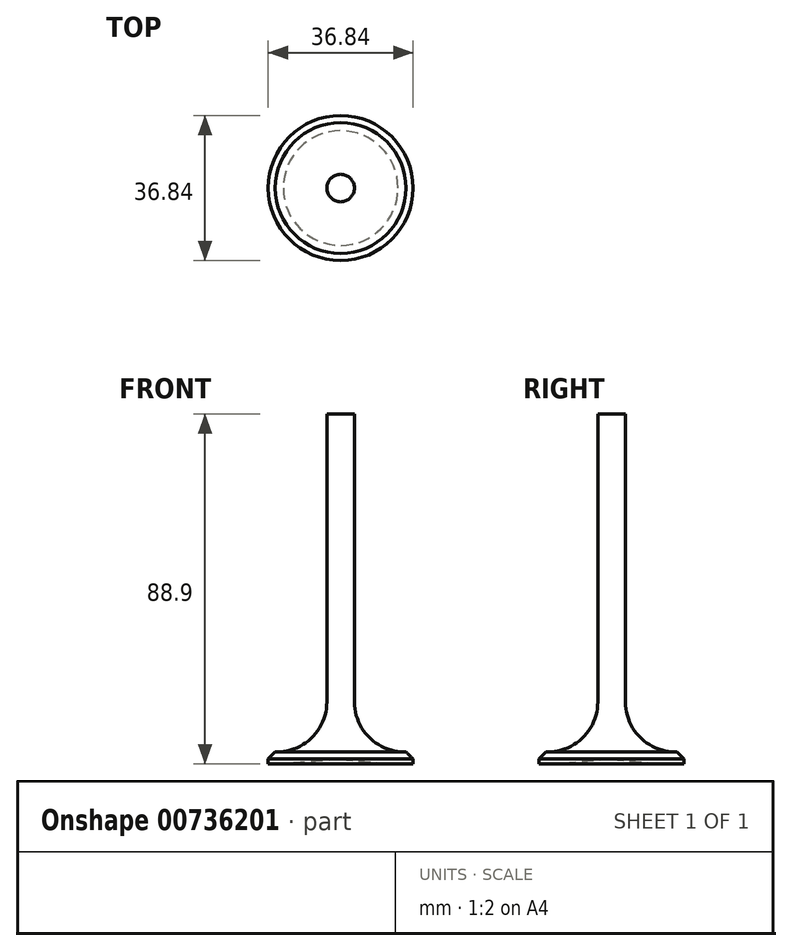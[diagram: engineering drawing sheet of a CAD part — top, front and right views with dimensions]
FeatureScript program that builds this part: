
annotation { "Feature Type Name" : "Feature", "Feature Type Description" : "" }
export const myFeature = defineFeature(function(context is Context, id is Id, definition is map)
    precondition{}
    {
        {
            var Q0;
            Q0=qCreatedBy(makeId("Front.planeOp"),FACE);
            var sketch = newSketch(context, id + "F0", { "sketchPlane" : qUnion([Q0])});
            skLineSegment(sketch, "E0", {"start": v(-14.56, 0) * mm, "end": v(-18.41, 0) * mm});
            skLineSegment(sketch, "E1", {"start": v(-18.41, 0) * mm, "end": v(-18.41, 1.27) * mm});
            skLineSegment(sketch, "E2", {"start": v(-18.41, 1.27) * mm, "end": v(-16.62, 3.07) * mm});
            skLineSegment(sketch, "E3", {"start": v(-16.62, 3.07) * mm, "end": v(-16.2, 3.07) * mm});
            skLineSegment(sketch, "E4", {"start": v(-3.5, 88.9) * mm, "end": v(0, 88.9) * mm});
            skLineSegment(sketch, "E5", {"start": v(-3.5, 88.9) * mm, "end": v(-3.5, 15.77) * mm});
            skLineSegment(sketch, "E6", {"start": v(0, 88.9) * mm, "end": v(0, 1.19) * mm});
            skPoint(sketch, "E7.MirrorCS.end.orphan", {"position": v(0, 88.9) * mm});
            skPoint(sketch, "E7.MirrorCS.start.orphan", {"position": v(3.5, 88.9) * mm});
            skPoint(sketch, "E8.MirrorCS.end.orphan", {"position": v(18.41, 0) * mm});
            skPoint(sketch, "E8.MirrorCS.start.orphan", {"position": v(0, 0) * mm});
            skPoint(sketch, "E9.orphan", {"position": v(0, 3.07) * mm});
            skPoint(sketch, "E10.visualSharp", {"position": v(-3.5, 3.07) * mm});
            skArc(sketch, "E10.filletArc", {"start": v(-16.2, 3.07) * mm, "mid": v(-7.22, 6.79) * mm, "end": v(-3.5, 15.77) * mm});
            skLineSegment(sketch, "E11", {"start": v(-14.56, 0) * mm, "end": v(0, 1.19) * mm});
            skSolve(sketch);
        }
        {
            var Q0;
            Q0=makeQuery(id+"F0.imprint","IMPRINT",FACE,{"disambiguationData":[TD([[makeQuery(id+"F0.imprint","IMPRINT",EDGE,{"derivedFrom":sQuery(id+"F0.wireOp",EDGE,"E0")}),-1.0]])]});
            var Q1;
            Q1=sQuery(id+"F0.wireOp",EDGE,"E6");
            revolve(context, id + "F1", {"surfaceOperationType" : NewSurfaceOperationType.NEW, "entities" : qUnion([Q0]), "axis" : qUnion([Q1]), "revolveType" : RevolveType.FULL});
        }
    });
